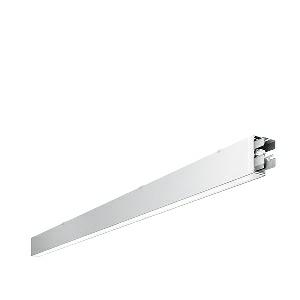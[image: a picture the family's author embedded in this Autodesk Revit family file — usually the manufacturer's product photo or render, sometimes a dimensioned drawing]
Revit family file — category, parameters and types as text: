
# Revit family: dotoo_line_-_dla_3000_830_d_sta_00807946_72b7
name_source: partatom
category: Lighting Fixtures
units: mm (PartAtom-declared; Revit-internal decimal feet)

## family parameters
Cut with Voids When Loaded = No
Host = Face
Light Source = No
Part Type = Normal
Room Calculation Point = No
Round Connector Dimension = Use Diameter
Shared = No

## types (1)
- DOTOO.line - DLA 3000/830/D STA (1 x LED, 2650 lm, 3000K)
    Apparent Load = 26 VA
    Approval mark = CE
    CIE Flux Codes = 67 91 98 100 100
    Color Rendering = 80-89
    Color Temperature = 3000K
    Control Gear = Electronic ballast
    Default Elevation = 1800 mm
    Description = DLA 3000/830/D|Surface-mounted luminaire.|light source: LED|work equipment: Adjustable electronic ballast, digital DALI|connected load: 220-240 V, 50/60 Hz|Power consumption: approx. 26 W|luminous flux: 2650 lm|luminous efficacy: 101 lm/W|light distribution: Direct|colour temperature: Warm white, ca. 3000 K|class of protection: I|technology: Continuously dimmable|mains lead: Connector|glare control: Prism aperture|special features: DALI Load 1x, TouchDIM - dimming via standard switch, Through-wired, up to 18 m on one mains connection, Flicker-free, Suitable as emergency lighting, Start luminaire with mains connection, Maintenance-friendly due to easily accessible ballasts|
    Frequency = 50 Hz
    Height = 110 mm
    Lamp = 1 x LED
    Lamp Light Flux = 2650 lm
    Lamp count = 1
    Length = 2250 mm
    Luminous efficacy = 102 lm/W
    Manufacturer = Waldmann
    ModVariant = No
    Model = 00807946
    Mounting Place = Ceiling
    Mounting Type = Surface mounted
    Number of Poles = 1
    OnlyDefault = Yes
    Power Factor = 1
    Product Name = DOTOO.line - DLA 3000/830/D STA
    Product group = Ceiling mounted luminaire
    ProductGroupID = 3
    Protection Class = Protection class I
    Protection Degree = IP 40
    RLX_Detail_Level = 1
    RLX_Emergency_Light_Flux = 0 lm
    RLX_Emergency_Type = 0
    RLX_Emergency_Type_DB = No
    RlxData = <blob elided: 20493 chars, md5=076a5f26>
    Socket = socket
    Standby Power = 0 W
    System Light Flux = 2650 lm
    System Power = 26 W
    Type Comments = Product without accessories
    Type Image = 114357000-00807934.jpg
    URL = http://relux.com
    VarID = ---
    Voltage = 230 V
    Voltage Range = 220-240 V
    Weight = 0.00 kg
    Width = 60 mm  [stored 0.19685 ft]

note: [stored X ft] marks values corroborated as IEEE doubles in the binary element streams (Revit-internal decimal feet)

## geometry (parser evidence)
native form markers: Blend x4, Sweep x12
no freeform markers — native parametric forms only
